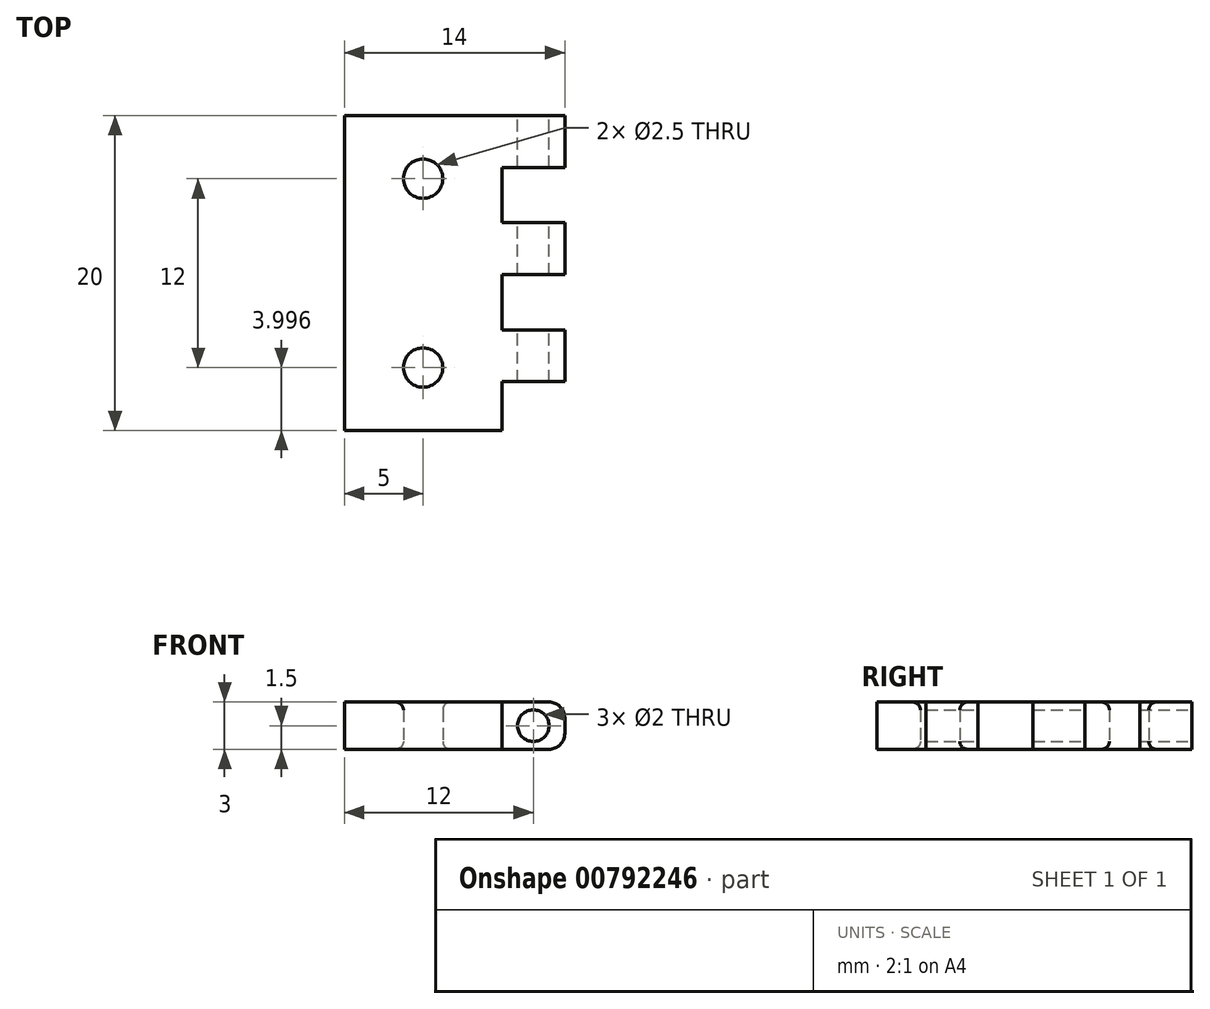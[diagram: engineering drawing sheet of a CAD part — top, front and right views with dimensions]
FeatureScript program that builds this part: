
annotation { "Feature Type Name" : "Feature", "Feature Type Description" : "" }
export const myFeature = defineFeature(function(context is Context, id is Id, definition is map)
    precondition{}
    {
        {
            var Q0;
            Q0=qCreatedBy(makeId("Top.planeOp"),FACE);
            var sketch = newSketch(context, id + "F0", { "sketchPlane" : qUnion([Q0])});
            skLineSegment(sketch, "E0.bottom", {"start": v(-10, 12.44) * mm, "end": v(0, 12.44) * mm});
            skLineSegment(sketch, "E0.top", {"start": v(-10, -7.56) * mm, "end": v(0, -7.56) * mm});
            skLineSegment(sketch, "E0.left", {"start": v(-10, 12.44) * mm, "end": v(-10, -7.56) * mm});
            skLineSegment(sketch, "E0.right", {"start": v(0, 9.14) * mm, "end": v(0, 5.64) * mm});
            skCircle(sketch, "E1", {"center": v(-5, -3.56) * mm, "radius": 1.25 * mm});
            skCircle(sketch, "E2", {"center": v(-5, 8.44) * mm, "radius": 1.25 * mm});
            skLineSegment(sketch, "E3.bottom", {"start": v(0, 12.44) * mm, "end": v(4, 12.44) * mm});
            skLineSegment(sketch, "E3.top", {"start": v(0, 9.14) * mm, "end": v(4, 9.14) * mm});
            skLineSegment(sketch, "E3.right", {"start": v(4, 12.44) * mm, "end": v(4, 9.14) * mm});
            skLineSegment(sketch, "E4.bottom", {"start": v(0, 5.64) * mm, "end": v(4, 5.64) * mm});
            skLineSegment(sketch, "E4.top", {"start": v(0, 2.34) * mm, "end": v(4, 2.34) * mm});
            skLineSegment(sketch, "E4.right", {"start": v(4, 5.64) * mm, "end": v(4, 2.34) * mm});
            skLineSegment(sketch, "E5.bottom", {"start": v(0, -1.16) * mm, "end": v(4, -1.16) * mm});
            skLineSegment(sketch, "E5.top", {"start": v(0, -4.46) * mm, "end": v(4, -4.46) * mm});
            skLineSegment(sketch, "E5.right", {"start": v(4, -1.16) * mm, "end": v(4, -4.46) * mm});
            skLineSegment(sketch, "E6.trimOffspring", {"start": v(0, 2.34) * mm, "end": v(0, -1.16) * mm});
            skLineSegment(sketch, "E7.trimOffspring", {"start": v(0, -4.46) * mm, "end": v(0, -7.56) * mm});
            skSolve(sketch);
        }
        {
            var Q0;
            Q0 = qSketchRegion(id + "F0", true);
            var Q1;
            Q1=makeQuery(id+"F0.imprint","IMPRINT",FACE,{"disambiguationData":[TD([[makeQuery(id+"F0.imprint","IMPRINT",EDGE,{"derivedFrom":sQuery(id+"F0.wireOp",EDGE,"E0.bottom")}),-1.0]])]});
            extrude(context, id + "F1", {"entities" : qUnion([Q0, Q1]), "depth" : 1.36 * mm, "offsetDistance" : 25 * mm});
        }
        {
            var Q0;
            Q0=makeQuery(id+"F1.opExtrude","CAP_EDGE",EDGE,{"disambiguationData":[OSD([sQuery(id+"F0.wireOp",EDGE,"E5.right")])],"isStart":false});
            var Q1;
            Q1=makeQuery(id+"F1.opExtrude","CAP_EDGE",EDGE,{"disambiguationData":[OSD([sQuery(id+"F0.wireOp",EDGE,"E4.right")])],"isStart":false});
            var Q2;
            Q2=makeQuery(id+"F1.opExtrude","CAP_EDGE",EDGE,{"disambiguationData":[OSD([sQuery(id+"F0.wireOp",EDGE,"E3.right")])],"isStart":false});
            var Q3;
            Q3=makeQuery(id+"F1.opExtrude","CAP_EDGE",EDGE,{"disambiguationData":[OSD([sQuery(id+"F0.wireOp",EDGE,"E5.right")])],"isStart":true});
            var Q4;
            Q4=makeQuery(id+"F1.opExtrude","CAP_EDGE",EDGE,{"disambiguationData":[OSD([sQuery(id+"F0.wireOp",EDGE,"E4.right")])],"isStart":true});
            var Q5;
            Q5=makeQuery(id+"F1.opExtrude","CAP_EDGE",EDGE,{"disambiguationData":[OSD([sQuery(id+"F0.wireOp",EDGE,"E3.right")])],"isStart":true});
            fillet(context, id + "F2", {"entities" : qUnion([Q0, Q1, Q2, Q3, Q4, Q5]), "radius" : 0.4 * mm, "tangentPropagation" : true, "allowEdgeOverflow" : false});
        }
        {
            var Q0;
            Q0=qCreatedBy(makeId("Front.planeOp"),FACE);
            var sketch = newSketch(context, id + "F3", { "sketchPlane" : qUnion([Q0])});
            skPoint(sketch, "E8", {"position": v(2, 0) * mm});
            skPoint(sketch, "E9", {"position": v(2, 1.5) * mm});
            skCircle(sketch, "E10", {"center": v(2, 1.5) * mm, "radius": 1 * mm});
            skSolve(sketch);
        }
        {
            var Q0;
            Q0=makeQuery(id+"F3.imprint","IMPRINT",FACE,{"disambiguationData":[TD([[makeQuery(id+"F3.imprint","IMPRINT",EDGE,{"derivedFrom":sQuery(id+"F3.wireOp",EDGE,"E10")}),1.0]])]});
            extrude(context, id + "F4", {"entities" : qUnion([Q0]), "endBound" : BoundingType.SYMMETRIC, "depth" : 37.66 * mm, "offsetDistance" : 25 * mm});
        }
        {
            var Q0;
            Q0=makeQuery(id+"F0.imprint","IMPRINT",FACE,{"disambiguationData":[TD([[makeQuery(id+"F0.imprint","IMPRINT",EDGE,{"derivedFrom":sQuery(id+"F0.wireOp",EDGE,"E0.bottom")}),-1.0]])]});
            extrude(context, id + "F5", {"entities" : qUnion([Q0]), "depth" : 3 * mm, "offsetDistance" : 25 * mm});
        }
        {
            var Q0;
            Q0=makeQuery(id+"F5.opExtrude","CAP_EDGE",EDGE,{"disambiguationData":[OSD([sQuery(id+"F0.wireOp",EDGE,"E5.right")])],"isStart":false});
            var Q1;
            Q1=makeQuery(id+"F5.opExtrude","CAP_EDGE",EDGE,{"disambiguationData":[OSD([sQuery(id+"F0.wireOp",EDGE,"E4.right")])],"isStart":false});
            var Q2;
            Q2=makeQuery(id+"F5.opExtrude","CAP_EDGE",EDGE,{"disambiguationData":[OSD([sQuery(id+"F0.wireOp",EDGE,"E3.right")])],"isStart":false});
            var Q3;
            Q3=makeQuery(id+"F5.opExtrude","CAP_EDGE",EDGE,{"disambiguationData":[OSD([sQuery(id+"F0.wireOp",EDGE,"E3.right")])],"isStart":true});
            var Q4;
            Q4=makeQuery(id+"F5.opExtrude","CAP_EDGE",EDGE,{"disambiguationData":[OSD([sQuery(id+"F0.wireOp",EDGE,"E4.right")])],"isStart":true});
            var Q5;
            Q5=makeQuery(id+"F5.opExtrude","CAP_EDGE",EDGE,{"disambiguationData":[OSD([sQuery(id+"F0.wireOp",EDGE,"E5.right")])],"isStart":true});
            fillet(context, id + "F6", {"entities" : qUnion([Q0, Q1, Q2, Q3, Q4, Q5]), "radius" : 1 * mm, "tangentPropagation" : true, "allowEdgeOverflow" : false});
        }
        {
            var Q0;
            Q0=makeQuery(id+"F4.opExtrude","SWEPT_BODY",BODY,{"disambiguationData":[OSD([sQuery(id+"F3.wireOp",EDGE,"E10")])]});
            var Q1;
            Q1=makeQuery(id+"F5.opExtrude","SWEPT_BODY",BODY,{"disambiguationData":[OSD([sQuery(id+"F0.wireOp",EDGE,"E0.bottom"),sQuery(id+"F0.wireOp",EDGE,"E0.top"),sQuery(id+"F0.wireOp",EDGE,"E0.left"),sQuery(id+"F0.wireOp",EDGE,"E0.right"),sQuery(id+"F0.wireOp",EDGE,"E1"),sQuery(id+"F0.wireOp",EDGE,"E2"),sQuery(id+"F0.wireOp",EDGE,"E3.bottom"),sQuery(id+"F0.wireOp",EDGE,"E3.top"),sQuery(id+"F0.wireOp",EDGE,"E3.right"),sQuery(id+"F0.wireOp",EDGE,"E4.bottom"),sQuery(id+"F0.wireOp",EDGE,"E4.top"),sQuery(id+"F0.wireOp",EDGE,"E4.right"),sQuery(id+"F0.wireOp",EDGE,"E5.bottom"),sQuery(id+"F0.wireOp",EDGE,"E5.top"),sQuery(id+"F0.wireOp",EDGE,"E5.right"),sQuery(id+"F0.wireOp",EDGE,"E6.trimOffspring"),sQuery(id+"F0.wireOp",EDGE,"E7.trimOffspring")])]});
            booleanBodies(context, id + "F7", {"operationType" : BooleanOperationType.SUBTRACTION, "tools" : qUnion([Q0]), "targets" : qUnion([Q1])});
        }
        {
            var Q0;
            Q0=makeQuery(id+"F1.opExtrude","SWEPT_BODY",BODY,{"disambiguationData":[OSD([sQuery(id+"F0.wireOp",EDGE,"E0.bottom"),sQuery(id+"F0.wireOp",EDGE,"E0.top"),sQuery(id+"F0.wireOp",EDGE,"E0.left"),sQuery(id+"F0.wireOp",EDGE,"E0.right"),sQuery(id+"F0.wireOp",EDGE,"E1"),sQuery(id+"F0.wireOp",EDGE,"E2"),sQuery(id+"F0.wireOp",EDGE,"E3.bottom"),sQuery(id+"F0.wireOp",EDGE,"E3.top"),sQuery(id+"F0.wireOp",EDGE,"E3.right"),sQuery(id+"F0.wireOp",EDGE,"E4.bottom"),sQuery(id+"F0.wireOp",EDGE,"E4.top"),sQuery(id+"F0.wireOp",EDGE,"E4.right"),sQuery(id+"F0.wireOp",EDGE,"E5.bottom"),sQuery(id+"F0.wireOp",EDGE,"E5.top"),sQuery(id+"F0.wireOp",EDGE,"E5.right"),sQuery(id+"F0.wireOp",EDGE,"E6.trimOffspring"),sQuery(id+"F0.wireOp",EDGE,"E7.trimOffspring")])]});
            deleteBodies(context, id + "F8", {"entities" : qUnion([Q0])});
        }
        {
            var Q0;
            Q0=makeQuery(id+"F5.opExtrude","CAP_EDGE",EDGE,{"disambiguationData":[OSD([sQuery(id+"F0.wireOp",EDGE,"E1")])],"isStart":false});
            var Q1;
            Q1=makeQuery(id+"F5.opExtrude","CAP_EDGE",EDGE,{"disambiguationData":[OSD([sQuery(id+"F0.wireOp",EDGE,"E2")])],"isStart":false});
            var Q2;
            Q2=makeQuery(id+"F5.opExtrude","CAP_EDGE",EDGE,{"disambiguationData":[OSD([sQuery(id+"F0.wireOp",EDGE,"E1")])],"isStart":true});
            var Q3;
            Q3=makeQuery(id+"F5.opExtrude","CAP_EDGE",EDGE,{"disambiguationData":[OSD([sQuery(id+"F0.wireOp",EDGE,"E2")])],"isStart":true});
            fillet(context, id + "F9", {"entities" : qUnion([Q0, Q1, Q2, Q3]), "radius" : 0.5 * mm, "tangentPropagation" : true, "allowEdgeOverflow" : false});
        }
    });
